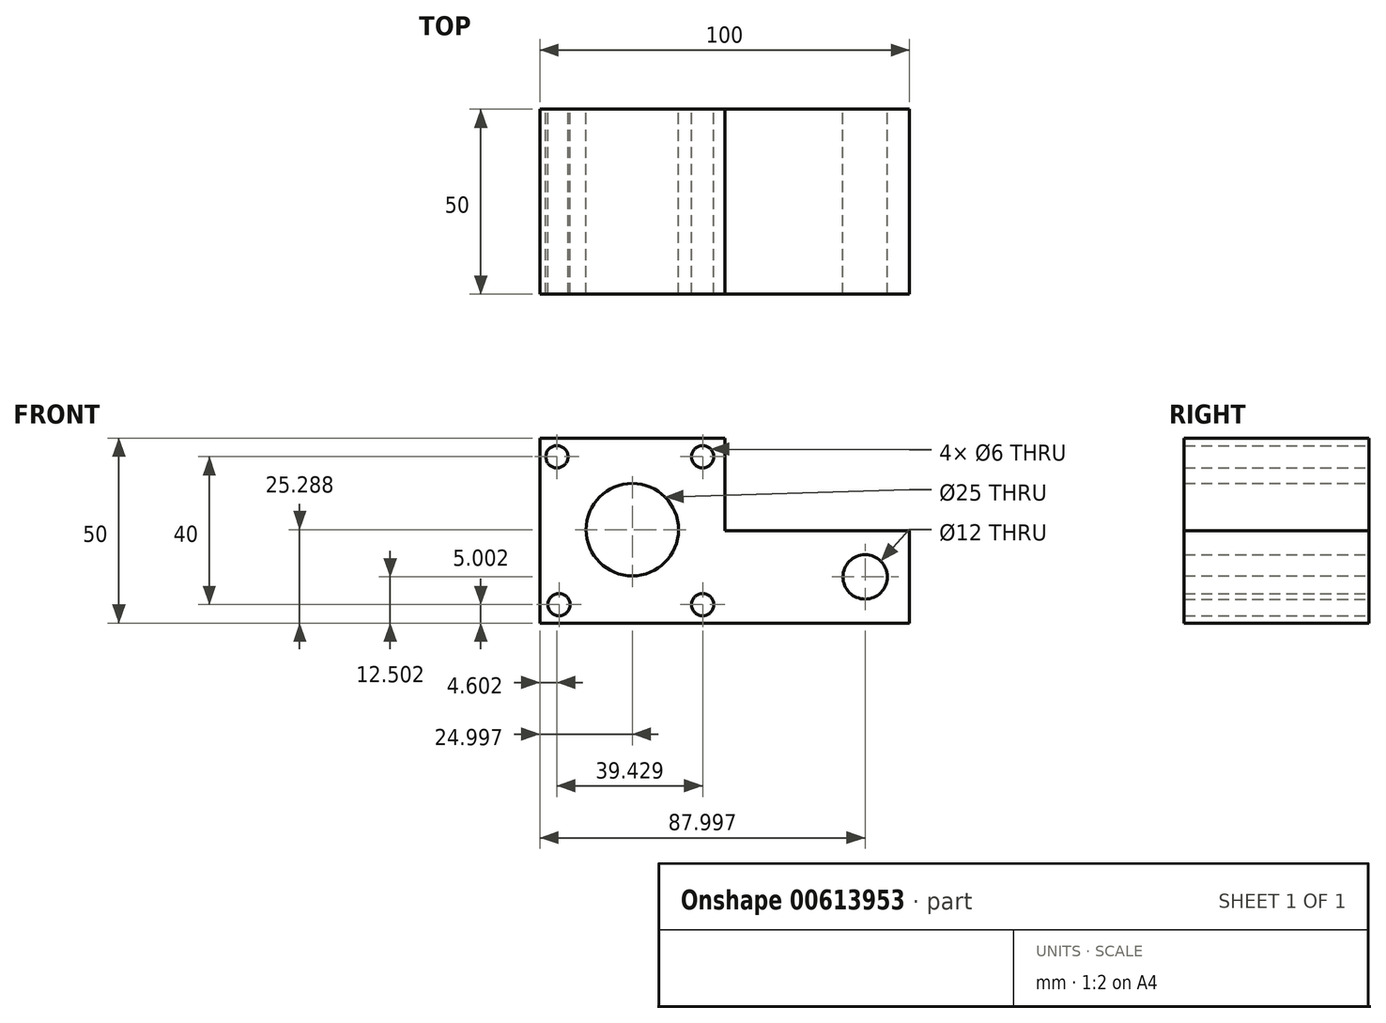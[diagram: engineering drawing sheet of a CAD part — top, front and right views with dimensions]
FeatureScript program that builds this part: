
annotation { "Feature Type Name" : "Feature", "Feature Type Description" : "" }
export const myFeature = defineFeature(function(context is Context, id is Id, definition is map)
    precondition{}
    {
        {
            var Q0;
            Q0=qCreatedBy(makeId("Front.planeOp"),FACE);
            var sketch = newSketch(context, id + "F0", { "sketchPlane" : qUnion([Q0])});
            skLineSegment(sketch, "E0", {"start": v(-34.4, 34.21) * mm, "end": v(-34.4, -15.79) * mm});
            skLineSegment(sketch, "E1", {"start": v(-34.4, -15.79) * mm, "end": v(65.6, -15.79) * mm});
            skLineSegment(sketch, "E2", {"start": v(-34.4, 34.21) * mm, "end": v(15.6, 34.21) * mm});
            skLineSegment(sketch, "E3", {"start": v(65.6, -15.79) * mm, "end": v(65.6, 9.21) * mm});
            skLineSegment(sketch, "E4", {"start": v(65.6, 9.21) * mm, "end": v(15.6, 9.21) * mm});
            skLineSegment(sketch, "E5", {"start": v(15.6, 9.21) * mm, "end": v(15.6, 34.21) * mm});
            skCircle(sketch, "E6", {"center": v(-9.4, 9.5) * mm, "radius": 12.5 * mm});
            skCircle(sketch, "E7", {"center": v(-29.79, 29.21) * mm, "radius": 3 * mm});
            skCircle(sketch, "E8", {"center": v(-29.21, -10.79) * mm, "radius": 3 * mm});
            skCircle(sketch, "E9", {"center": v(9.64, -10.79) * mm, "radius": 3 * mm});
            skCircle(sketch, "E10", {"center": v(9.64, 29.21) * mm, "radius": 3 * mm});
            skCircle(sketch, "E11", {"center": v(53.6, -3.29) * mm, "radius": 6 * mm});
            skSolve(sketch);
        }
        {
            var Q0;
            Q0=makeQuery(id+"F0.imprint","IMPRINT",FACE,{"disambiguationData":[TD([[makeQuery(id+"F0.imprint","IMPRINT",EDGE,{"derivedFrom":sQuery(id+"F0.wireOp",EDGE,"E0")}),1.0]])]});
            extrude(context, id + "F1", {"entities" : qUnion([Q0]), "depth" : 50 * mm, "offsetDistance" : 25 * mm});
        }
    });
